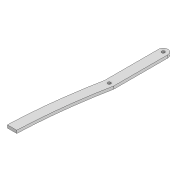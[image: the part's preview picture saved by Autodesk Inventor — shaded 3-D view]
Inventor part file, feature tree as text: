
AUTODESK INVENTOR PART (.ipt)
format: ipt  version: 2022 (Build 260153000, 153)  size: 109,056 bytes
history: native  units: mm
features: extrude x2, sketch x2
ambient origin geometry x8: Origin, YZ Plane, XZ Plane, XY Plane, X Axis, Y Axis, Z Axis, Center Point
bodies: Solid1 (feature_tree)
feature tree (4):
  extrude  "Extrusion1"  Depth=3.3mm
  extrude  "Extrusion2"  Depth=288.984mm
  sketch  "Sketch1"  dims[d0=3.3mm d1=3.3mm]
  sketch  "Sketch2"  dims[d2=10.0mm d3=288.984mm d6=3.0mm d7=0.0mm d14=3.3mm d15=231.585mm d18=600.0mm d19=600.0mm d20=10.0mm d21=0.0mm]
